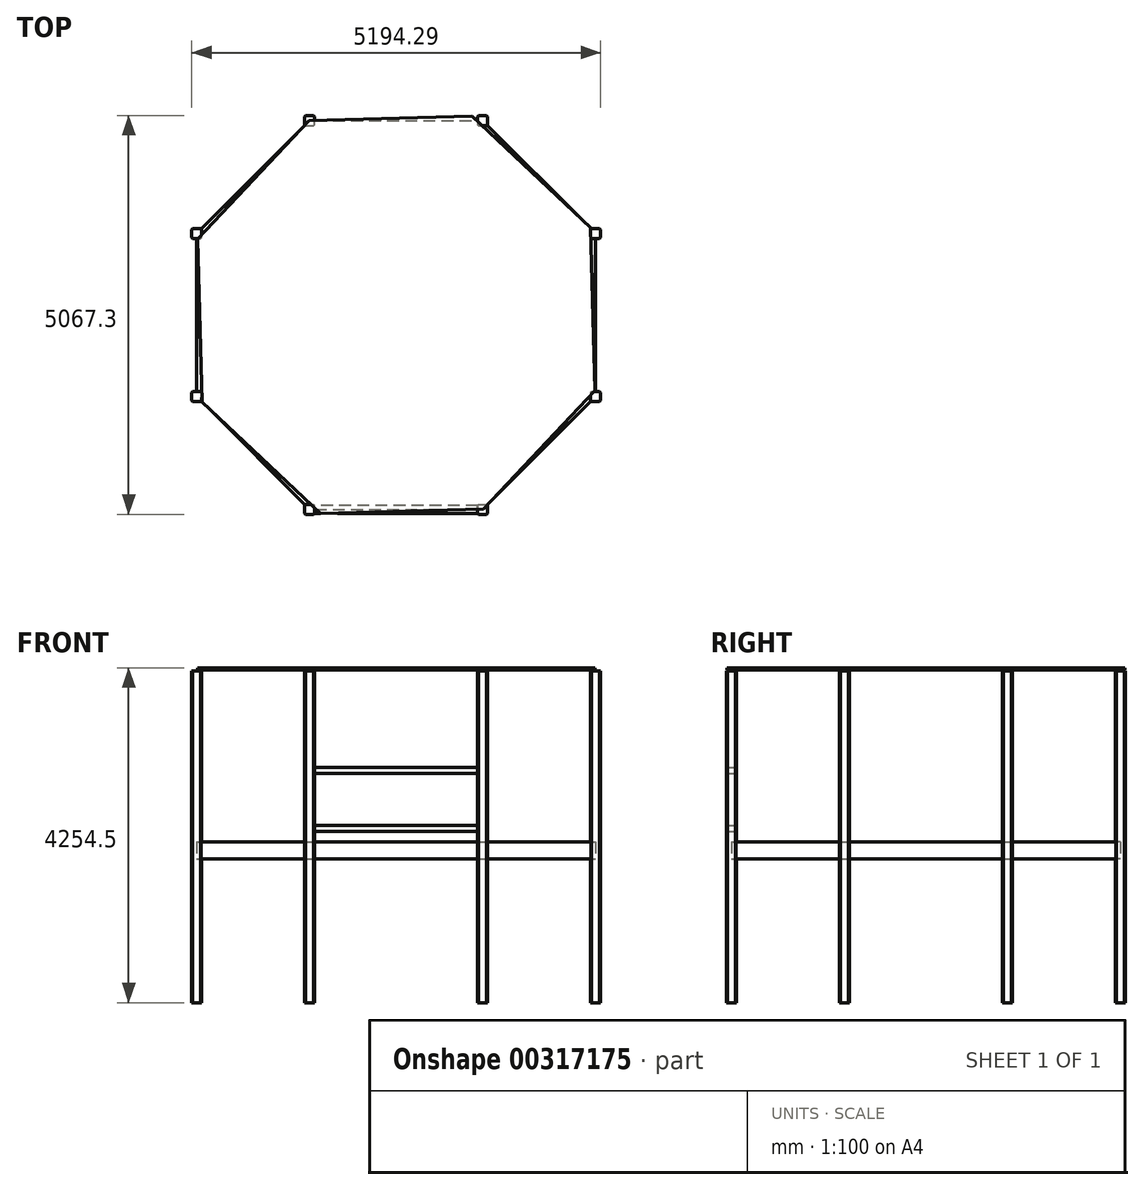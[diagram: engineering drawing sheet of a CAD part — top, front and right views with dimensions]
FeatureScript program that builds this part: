
annotation { "Feature Type Name" : "Feature", "Feature Type Description" : "" }
export const myFeature = defineFeature(function(context is Context, id is Id, definition is map)
    precondition{}
    {
        {
            var Q0;
            Q0=qCreatedBy(makeId("Top.planeOp"),FACE);
            var sketch = newSketch(context, id + "F0", { "sketchPlane" : qUnion([Q0])});
            skLineSegment(sketch, "E0", {"start": v(-238.21, 928.65) * mm, "end": v(-238.21, 827.05) * mm});
            skLineSegment(sketch, "E1", {"start": v(-238.21, 827.05) * mm, "end": v(-225.51, 814.35) * mm});
            skLineSegment(sketch, "E2", {"start": v(-225.51, 814.35) * mm, "end": v(-123.91, 814.35) * mm});
            skLineSegment(sketch, "E3", {"start": v(-123.91, 814.35) * mm, "end": v(-111.21, 827.05) * mm});
            skLineSegment(sketch, "E4", {"start": v(-111.21, 827.05) * mm, "end": v(-111.21, 928.65) * mm});
            skLineSegment(sketch, "E5", {"start": v(-111.21, 928.65) * mm, "end": v(-123.91, 941.35) * mm});
            skLineSegment(sketch, "E6", {"start": v(-238.21, 928.65) * mm, "end": v(-225.51, 941.35) * mm});
            skLineSegment(sketch, "E7", {"start": v(-225.51, 941.35) * mm, "end": v(-123.91, 941.35) * mm});
            skLineSegment(sketch, "E8", {"start": v(4829.09, 928.65) * mm, "end": v(4829.09, 827.05) * mm});
            skLineSegment(sketch, "E9", {"start": v(4829.09, 827.05) * mm, "end": v(4841.78, 814.35) * mm});
            skLineSegment(sketch, "E10", {"start": v(4841.78, 814.35) * mm, "end": v(4943.38, 814.35) * mm});
            skLineSegment(sketch, "E11", {"start": v(4943.38, 814.35) * mm, "end": v(4956.08, 827.05) * mm});
            skLineSegment(sketch, "E12", {"start": v(4956.08, 827.05) * mm, "end": v(4956.08, 928.65) * mm});
            skLineSegment(sketch, "E13", {"start": v(4956.08, 928.65) * mm, "end": v(4943.38, 941.35) * mm});
            skLineSegment(sketch, "E14", {"start": v(4829.09, 928.65) * mm, "end": v(4841.78, 941.35) * mm});
            skLineSegment(sketch, "E15", {"start": v(4841.78, 941.35) * mm, "end": v(4943.38, 941.35) * mm});
            skLineSegment(sketch, "E16", {"start": v(-111.21, 928.65) * mm, "end": v(4829.09, 928.65) * mm, "construction": true});
            skLineSegment(sketch, "E17", {"start": v(-238.21, -1141.45) * mm, "end": v(-238.21, -1243.05) * mm});
            skLineSegment(sketch, "E18", {"start": v(-238.21, -1243.05) * mm, "end": v(-225.51, -1255.75) * mm});
            skLineSegment(sketch, "E19", {"start": v(-225.51, -1255.75) * mm, "end": v(-123.91, -1255.75) * mm});
            skLineSegment(sketch, "E20", {"start": v(-123.91, -1255.75) * mm, "end": v(-111.21, -1243.05) * mm});
            skLineSegment(sketch, "E21", {"start": v(-111.21, -1243.05) * mm, "end": v(-111.21, -1141.45) * mm});
            skLineSegment(sketch, "E22", {"start": v(-111.21, -1141.45) * mm, "end": v(-123.91, -1128.75) * mm});
            skLineSegment(sketch, "E23", {"start": v(-238.21, -1141.45) * mm, "end": v(-225.51, -1128.75) * mm});
            skLineSegment(sketch, "E24", {"start": v(-225.51, -1128.75) * mm, "end": v(-123.91, -1128.75) * mm});
            skLineSegment(sketch, "E25", {"start": v(4829.09, -1141.45) * mm, "end": v(4829.09, -1243.05) * mm});
            skLineSegment(sketch, "E26", {"start": v(4829.09, -1243.05) * mm, "end": v(4841.78, -1255.75) * mm});
            skLineSegment(sketch, "E27", {"start": v(4841.78, -1255.75) * mm, "end": v(4943.38, -1255.75) * mm});
            skLineSegment(sketch, "E28", {"start": v(4943.38, -1255.75) * mm, "end": v(4956.08, -1243.05) * mm});
            skLineSegment(sketch, "E29", {"start": v(4956.08, -1243.05) * mm, "end": v(4956.08, -1141.45) * mm});
            skLineSegment(sketch, "E30", {"start": v(4956.08, -1141.45) * mm, "end": v(4943.38, -1128.75) * mm});
            skLineSegment(sketch, "E31", {"start": v(4829.09, -1141.45) * mm, "end": v(4841.78, -1128.75) * mm});
            skLineSegment(sketch, "E32", {"start": v(4841.78, -1128.75) * mm, "end": v(4943.38, -1128.75) * mm});
            skLineSegment(sketch, "E33", {"start": v(-111.21, -1141.45) * mm, "end": v(4829.09, -1141.45) * mm, "construction": true});
            skLineSegment(sketch, "E34", {"start": v(-123.91, 814.35) * mm, "end": v(-123.91, -1128.75) * mm, "construction": true});
            skLineSegment(sketch, "E35", {"start": v(1196.89, 2363.75) * mm, "end": v(1196.89, 2262.15) * mm});
            skLineSegment(sketch, "E36", {"start": v(1196.89, 2262.15) * mm, "end": v(1209.59, 2249.45) * mm});
            skLineSegment(sketch, "E37", {"start": v(1209.59, 2249.45) * mm, "end": v(1311.19, 2249.45) * mm});
            skLineSegment(sketch, "E38", {"start": v(1311.19, 2249.45) * mm, "end": v(1323.89, 2262.15) * mm});
            skLineSegment(sketch, "E39", {"start": v(1323.89, 2262.15) * mm, "end": v(1323.89, 2363.75) * mm});
            skLineSegment(sketch, "E40", {"start": v(1323.89, 2363.75) * mm, "end": v(1311.19, 2376.45) * mm});
            skLineSegment(sketch, "E41", {"start": v(1196.89, 2363.75) * mm, "end": v(1209.59, 2376.45) * mm});
            skLineSegment(sketch, "E42", {"start": v(1209.59, 2376.45) * mm, "end": v(1311.19, 2376.45) * mm});
            skLineSegment(sketch, "E43", {"start": v(3393.99, 2363.75) * mm, "end": v(3393.99, 2262.15) * mm});
            skLineSegment(sketch, "E44", {"start": v(3393.99, 2262.15) * mm, "end": v(3406.68, 2249.45) * mm});
            skLineSegment(sketch, "E45", {"start": v(3406.68, 2249.45) * mm, "end": v(3508.28, 2249.45) * mm});
            skLineSegment(sketch, "E46", {"start": v(3508.28, 2249.45) * mm, "end": v(3520.98, 2262.15) * mm});
            skLineSegment(sketch, "E47", {"start": v(3520.98, 2262.15) * mm, "end": v(3520.98, 2363.75) * mm});
            skLineSegment(sketch, "E48", {"start": v(3520.98, 2363.75) * mm, "end": v(3508.28, 2376.45) * mm});
            skLineSegment(sketch, "E49", {"start": v(3393.99, 2363.75) * mm, "end": v(3406.68, 2376.45) * mm});
            skLineSegment(sketch, "E50", {"start": v(3406.68, 2376.45) * mm, "end": v(3508.28, 2376.45) * mm});
            skLineSegment(sketch, "E51", {"start": v(1323.89, 2363.75) * mm, "end": v(3393.99, 2363.75) * mm, "construction": true});
            skLineSegment(sketch, "E52", {"start": v(1196.89, -2576.55) * mm, "end": v(1196.89, -2678.15) * mm});
            skLineSegment(sketch, "E53", {"start": v(1196.89, -2678.15) * mm, "end": v(1209.59, -2690.85) * mm});
            skLineSegment(sketch, "E54", {"start": v(1209.59, -2690.85) * mm, "end": v(1311.19, -2690.85) * mm});
            skLineSegment(sketch, "E55", {"start": v(1311.19, -2690.85) * mm, "end": v(1323.89, -2678.15) * mm});
            skLineSegment(sketch, "E56", {"start": v(1323.89, -2678.15) * mm, "end": v(1323.89, -2576.55) * mm});
            skLineSegment(sketch, "E57", {"start": v(1323.89, -2576.55) * mm, "end": v(1311.19, -2563.85) * mm});
            skLineSegment(sketch, "E58", {"start": v(1196.89, -2576.55) * mm, "end": v(1209.59, -2563.85) * mm});
            skLineSegment(sketch, "E59", {"start": v(1209.59, -2563.85) * mm, "end": v(1311.19, -2563.85) * mm});
            skLineSegment(sketch, "E60", {"start": v(3393.99, -2576.55) * mm, "end": v(3393.99, -2678.15) * mm});
            skLineSegment(sketch, "E61", {"start": v(3393.99, -2678.15) * mm, "end": v(3406.68, -2690.85) * mm});
            skLineSegment(sketch, "E62", {"start": v(3406.68, -2690.85) * mm, "end": v(3508.28, -2690.85) * mm});
            skLineSegment(sketch, "E63", {"start": v(3508.28, -2690.85) * mm, "end": v(3520.98, -2678.15) * mm});
            skLineSegment(sketch, "E64", {"start": v(3520.98, -2678.15) * mm, "end": v(3520.98, -2576.55) * mm});
            skLineSegment(sketch, "E65", {"start": v(3520.98, -2576.55) * mm, "end": v(3508.28, -2563.85) * mm});
            skLineSegment(sketch, "E66", {"start": v(3393.99, -2576.55) * mm, "end": v(3406.68, -2563.85) * mm});
            skLineSegment(sketch, "E67", {"start": v(3406.68, -2563.85) * mm, "end": v(3508.28, -2563.85) * mm});
            skLineSegment(sketch, "E68", {"start": v(1323.89, -2576.55) * mm, "end": v(3393.99, -2576.55) * mm, "construction": true});
            skLineSegment(sketch, "E69", {"start": v(2358.94, 2363.75) * mm, "end": v(2358.94, 928.65) * mm, "construction": true});
            skLineSegment(sketch, "E70", {"start": v(2358.94, -1141.45) * mm, "end": v(2358.94, -2576.55) * mm, "construction": true});
            skLineSegment(sketch, "E71", {"start": v(-174.71, 814.35) * mm, "end": v(-174.71, -1128.75) * mm});
            skLineSegment(sketch, "E72", {"start": v(-117.56, -1249.4) * mm, "end": v(1203.24, -2570.2) * mm});
            skLineSegment(sketch, "E73", {"start": v(-117.56, 935) * mm, "end": v(1203.24, 2255.8) * mm});
            skLineSegment(sketch, "E74", {"start": v(3514.63, 2255.8) * mm, "end": v(4835.43, 935) * mm});
            skLineSegment(sketch, "E75", {"start": v(4892.58, 814.35) * mm, "end": v(4892.58, -1128.75) * mm});
            skLineSegment(sketch, "E76", {"start": v(4835.43, -1249.4) * mm, "end": v(3514.63, -2570.2) * mm});
            skLineSegment(sketch, "E77", {"start": v(1323.89, 2312.95) * mm, "end": v(3393.99, 2312.95) * mm});
            skLineSegment(sketch, "E78", {"start": v(1323.89, -2627.35) * mm, "end": v(3393.99, -2627.35) * mm});
            skSolve(sketch);
        }
        {
            var Q0;
            Q0=makeQuery(id+"F0.imprint","IMPRINT",FACE,{"disambiguationData":[TD([[makeQuery(id+"F0.imprint","IMPRINT",EDGE,{"derivedFrom":sQuery(id+"F0.wireOp",EDGE,"E0")}),1.0]])]});
            var Q1;
            Q1=makeQuery(id+"F0.imprint","IMPRINT",FACE,{"disambiguationData":[TD([[makeQuery(id+"F0.imprint","IMPRINT",EDGE,{"derivedFrom":sQuery(id+"F0.wireOp",EDGE,"E17")}),1.0]])]});
            var Q2;
            {var subQ1=sQuery(id+"F0.wireOp",EDGE,"E52");Q2=makeQuery(id+"F0.imprint","IMPRINT",FACE,{"disambiguationData":[TD([[makeQuery(id+"F0.imprint","IMPRINT",EDGE,{"derivedFrom":subQ1}),1.0]])]});}
            var Q3;
            {var subQ0=sQuery(id+"F0.wireOp",EDGE,"E61");Q3=makeQuery(id+"F0.imprint","IMPRINT",FACE,{"disambiguationData":[TD([[makeQuery(id+"F0.imprint","IMPRINT",EDGE,{"derivedFrom":subQ0}),1.0]])]});}
            var Q4;
            {var subQ3=sQuery(id+"F0.wireOp",EDGE,"E25");Q4=makeQuery(id+"F0.imprint","IMPRINT",FACE,{"disambiguationData":[TD([[makeQuery(id+"F0.imprint","IMPRINT",EDGE,{"derivedFrom":subQ3}),1.0]])]});}
            var Q5;
            {var subQ4=sQuery(id+"F0.wireOp",EDGE,"E8");Q5=makeQuery(id+"F0.imprint","IMPRINT",FACE,{"disambiguationData":[TD([[makeQuery(id+"F0.imprint","IMPRINT",EDGE,{"derivedFrom":subQ4}),1.0]])]});}
            var Q6;
            {var subQ1=sQuery(id+"F0.wireOp",EDGE,"E44");Q6=makeQuery(id+"F0.imprint","IMPRINT",FACE,{"disambiguationData":[TD([[makeQuery(id+"F0.imprint","IMPRINT",EDGE,{"derivedFrom":subQ1}),1.0]])]});}
            var Q7;
            {var subQ3=sQuery(id+"F0.wireOp",EDGE,"E35");Q7=makeQuery(id+"F0.imprint","IMPRINT",FACE,{"disambiguationData":[TD([[makeQuery(id+"F0.imprint","IMPRINT",EDGE,{"derivedFrom":subQ3}),1.0]])]});}
            extrude(context, id + "F1", {"entities" : qUnion([Q0, Q1, Q2, Q3, Q4, Q5, Q6, Q7]), "depth" : 2387.6 * mm, "hasSecondDirection" : true, "secondDirectionOppositeDirection" : true, "secondDirectionDepth" : 1828.8 * mm});
        }
        {
            var Q0;
            {var subQ26=sQuery(id+"F0.wireOp",EDGE,"E3");Q0=makeQuery(id+"F0.imprint","IMPRINT",FACE,{"disambiguationData":[TD([[makeQuery(id+"F0.imprint","IMPRINT",EDGE,{"derivedFrom":subQ26}),-1.0]])]});}
            extrude(context, id + "F2", {"entities" : qUnion([Q0]), "depth" : 215.9 * mm});
        }
        {
            var Q0;
            Q0=makeQuery(id+"F1.opExtrude","SWEPT_FACE",FACE,{"disambiguationData":[OSD([sQuery(id+"F0.wireOp",EDGE,"E56")])]});
            var sketch = newSketch(context, id + "F3", { "sketchPlane" : qUnion([Q0])});
            skLineSegment(sketch, "E79", {"start": v(-2576.55, 218.63) * mm, "end": v(-2678.15, 218.63) * mm, "construction": true});
            skLineSegment(sketch, "E80", {"start": v(-2627.35, 218.63) * mm, "end": v(-2627.35, 345.63) * mm, "construction": true});
            skLineSegment(sketch, "E81.bottom", {"start": v(-2678.15, 345.63) * mm, "end": v(-2576.55, 345.63) * mm});
            skLineSegment(sketch, "E81.top", {"start": v(-2678.15, 421.83) * mm, "end": v(-2576.55, 421.83) * mm});
            skLineSegment(sketch, "E81.left", {"start": v(-2678.15, 345.63) * mm, "end": v(-2678.15, 421.83) * mm});
            skLineSegment(sketch, "E81.right", {"start": v(-2576.55, 345.63) * mm, "end": v(-2576.55, 421.83) * mm});
            skLineSegment(sketch, "E82", {"start": v(-2627.35, 421.83) * mm, "end": v(-2627.35, 1082.23) * mm, "construction": true});
            skLineSegment(sketch, "E83.bottom", {"start": v(-2678.15, 1082.23) * mm, "end": v(-2576.55, 1082.23) * mm});
            skLineSegment(sketch, "E83.top", {"start": v(-2678.15, 1158.43) * mm, "end": v(-2576.55, 1158.43) * mm});
            skLineSegment(sketch, "E83.left", {"start": v(-2678.15, 1082.23) * mm, "end": v(-2678.15, 1158.43) * mm});
            skLineSegment(sketch, "E83.right", {"start": v(-2576.55, 1082.23) * mm, "end": v(-2576.55, 1158.43) * mm});
            skSolve(sketch);
        }
        {
            var Q0;
            Q0=makeQuery(id+"F3.imprint","IMPRINT",FACE,{"disambiguationData":[TD([[makeQuery(id+"F3.imprint","IMPRINT",EDGE,{"derivedFrom":sQuery(id+"F3.wireOp",EDGE,"E83.bottom")}),1.0]])]});
            var Q1;
            Q1=makeQuery(id+"F3.imprint","IMPRINT",FACE,{"disambiguationData":[TD([[makeQuery(id+"F3.imprint","IMPRINT",EDGE,{"derivedFrom":sQuery(id+"F3.wireOp",EDGE,"E81.bottom")}),1.0]])]});
            extrude(context, id + "F4", {"entities" : qUnion([Q0, Q1]), "depth" : 2070.1 * mm});
        }
        {
            var Q0;
            Q0=makeQuery(id+"F2.opExtrude","CAP_FACE",FACE,{"disambiguationData":[OSD([sQuery(id+"F0.wireOp",EDGE,"E2"),sQuery(id+"F0.wireOp",EDGE,"E3"),sQuery(id+"F0.wireOp",EDGE,"E4"),sQuery(id+"F0.wireOp",EDGE,"E5"),sQuery(id+"F0.wireOp",EDGE,"E8"),sQuery(id+"F0.wireOp",EDGE,"E9"),sQuery(id+"F0.wireOp",EDGE,"E10"),sQuery(id+"F0.wireOp",EDGE,"E14"),sQuery(id+"F0.wireOp",EDGE,"E20"),sQuery(id+"F0.wireOp",EDGE,"E21"),sQuery(id+"F0.wireOp",EDGE,"E22"),sQuery(id+"F0.wireOp",EDGE,"E24"),sQuery(id+"F0.wireOp",EDGE,"E25"),sQuery(id+"F0.wireOp",EDGE,"E26"),sQuery(id+"F0.wireOp",EDGE,"E31"),sQuery(id+"F0.wireOp",EDGE,"E32"),sQuery(id+"F0.wireOp",EDGE,"E36"),sQuery(id+"F0.wireOp",EDGE,"E37"),sQuery(id+"F0.wireOp",EDGE,"E38"),sQuery(id+"F0.wireOp",EDGE,"E39"),sQuery(id+"F0.wireOp",EDGE,"E43"),sQuery(id+"F0.wireOp",EDGE,"E44"),sQuery(id+"F0.wireOp",EDGE,"E45"),sQuery(id+"F0.wireOp",EDGE,"E46"),sQuery(id+"F0.wireOp",EDGE,"E56"),sQuery(id+"F0.wireOp",EDGE,"E57"),sQuery(id+"F0.wireOp",EDGE,"E58"),sQuery(id+"F0.wireOp",EDGE,"E59"),sQuery(id+"F0.wireOp",EDGE,"E60"),sQuery(id+"F0.wireOp",EDGE,"E65"),sQuery(id+"F0.wireOp",EDGE,"E66"),sQuery(id+"F0.wireOp",EDGE,"E67"),sQuery(id+"F0.wireOp",EDGE,"E71"),sQuery(id+"F0.wireOp",EDGE,"E72"),sQuery(id+"F0.wireOp",EDGE,"E73"),sQuery(id+"F0.wireOp",EDGE,"E74"),sQuery(id+"F0.wireOp",EDGE,"E75"),sQuery(id+"F0.wireOp",EDGE,"E76"),sQuery(id+"F0.wireOp",EDGE,"E77"),sQuery(id+"F0.wireOp",EDGE,"E78")])],"isStart":false});
            var sketch = newSketch(context, id + "F5", { "sketchPlane" : qUnion([Q0])});
            skPoint(sketch, "E84", {"position": v(2358.94, -157.2) * mm});
            skPoint(sketch, "E84.positionSnap0", {"position": v(2358.94, 2312.95) * mm});
            skPoint(sketch, "E84.positionSnap1", {"position": v(-174.71, -157.2) * mm});
            skCircle(sketch, "E85.cCircle", {"center": v(2358.94, -157.2) * mm, "radius": 2498.83 * mm, "construction": true});
            skPoint(sketch, "E85.cCircle.perimeterSnap0", {"position": v(542.84, 1595.4) * mm});
            skLineSegment(sketch, "E85.0", {"start": v(-168.1, 806.92) * mm, "end": v(1253.78, 2311.43) * mm});
            skLineSegment(sketch, "E85.1", {"start": v(1253.78, 2311.43) * mm, "end": v(3323.06, 2369.84) * mm});
            skLineSegment(sketch, "E85.2", {"start": v(3323.06, 2369.84) * mm, "end": v(4827.56, 947.95) * mm});
            skLineSegment(sketch, "E85.3", {"start": v(4827.56, 947.95) * mm, "end": v(4885.98, -1121.32) * mm});
            skLineSegment(sketch, "E85.4", {"start": v(4885.98, -1121.32) * mm, "end": v(3464.09, -2625.83) * mm});
            skLineSegment(sketch, "E85.5", {"start": v(3464.09, -2625.83) * mm, "end": v(1394.81, -2684.25) * mm});
            skLineSegment(sketch, "E85.6", {"start": v(1394.81, -2684.25) * mm, "end": v(-109.7, -1262.35) * mm});
            skLineSegment(sketch, "E85.7", {"start": v(-109.7, -1262.35) * mm, "end": v(-168.1, 806.92) * mm});
            skPoint(sketch, "E85.0.midPoint", {"position": v(542.84, 1559.18) * mm});
            skPoint(sketch, "E85.0.midPoint.positionSnap0", {"position": v(542.84, 1595.4) * mm});
            skSolve(sketch);
        }
        {
            var Q0;
            Q0 = qSketchRegion(id + "F5", true);
            extrude(context, id + "F6", {"entities" : qUnion([Q0]), "depth" : 25.4 * mm});
        }
        {
            var Q0;
            Q0=makeQuery(id+"F6.opExtrude","SWEPT_BODY",BODY,{"disambiguationData":[OSD([sQuery(id+"F5.wireOp",EDGE,"E85.0"),sQuery(id+"F5.wireOp",EDGE,"E85.1"),sQuery(id+"F5.wireOp",EDGE,"E85.2"),sQuery(id+"F5.wireOp",EDGE,"E85.3"),sQuery(id+"F5.wireOp",EDGE,"E85.4"),sQuery(id+"F5.wireOp",EDGE,"E85.5"),sQuery(id+"F5.wireOp",EDGE,"E85.6"),sQuery(id+"F5.wireOp",EDGE,"E85.7")])]});
            transform(context, id + "F7", {"entities" : qUnion([Q0]), "transformType" : TransformType.TRANSLATION_3D, "dx" : 0 * mm, "dy" : 0 * mm, "dz" : 2184.4 * mm, "makeCopy" : false});
        }
    });
